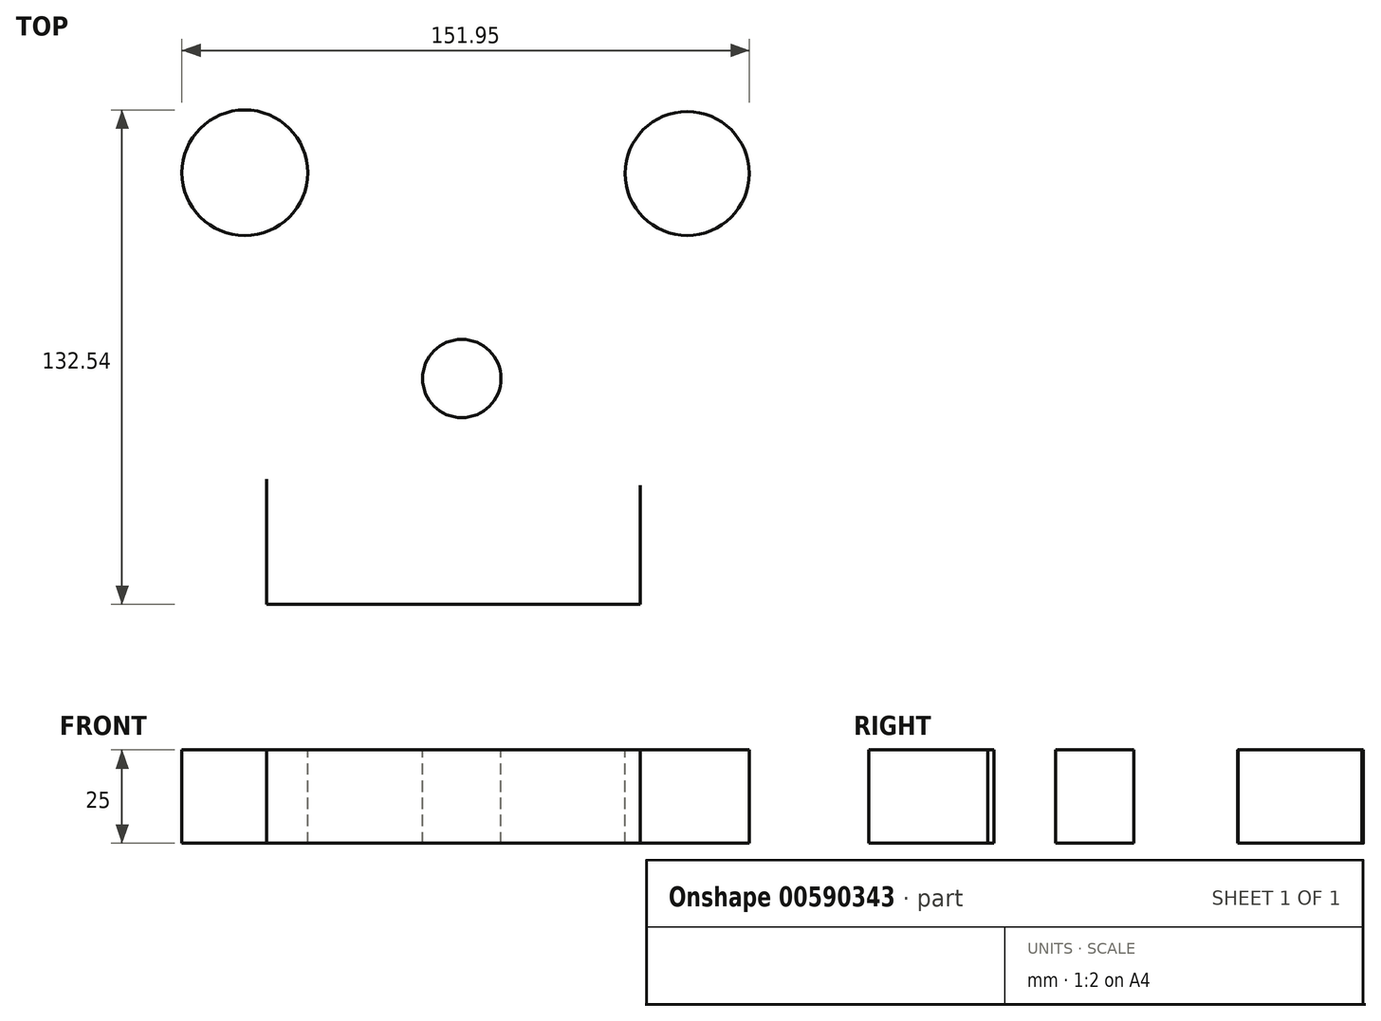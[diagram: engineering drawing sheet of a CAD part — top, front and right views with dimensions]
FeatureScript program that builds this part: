
annotation { "Feature Type Name" : "Feature", "Feature Type Description" : "" }
export const myFeature = defineFeature(function(context is Context, id is Id, definition is map)
    precondition{}
    {
        {
            var Q0;
            Q0=qCreatedBy(makeId("Top.planeOp"),FACE);
            var sketch = newSketch(context, id + "F0", { "sketchPlane" : qUnion([Q0])});
            skCircle(sketch, "E0", {"center": v(-58.13, 55.14) * mm, "radius": 16.83 * mm});
            skCircle(sketch, "E1", {"center": v(60.37, 54.96) * mm, "radius": 16.62 * mm});
            skCircle(sketch, "E2", {"center": v(0, 0) * mm, "radius": 10.5 * mm});
            skLineSegment(sketch, "E3", {"start": v(-52.28, -26.97) * mm, "end": v(-52.28, -60.56) * mm});
            skLineSegment(sketch, "E4", {"start": v(-52.28, -60.56) * mm, "end": v(47.74, -60.56) * mm});
            skLineSegment(sketch, "E5", {"start": v(47.74, -60.56) * mm, "end": v(47.74, -28.64) * mm});
            skSolve(sketch);
        }
        {
            var Q0;
            Q0=sQuery(id+"F0.wireOp",EDGE,"E3");
            var Q1;
            Q1=sQuery(id+"F0.wireOp",EDGE,"E4");
            var Q2;
            Q2=sQuery(id+"F0.wireOp",EDGE,"E5");
            var Q3;
            Q3=sQuery(id+"F0.wireOp",EDGE,"E2");
            var Q4;
            Q4=sQuery(id+"F0.wireOp",EDGE,"E0");
            var Q5;
            Q5=sQuery(id+"F0.wireOp",EDGE,"E1");
            extrude(context, id + "F1", {"bodyType" : ToolBodyType.SURFACE, "surfaceEntities" : qUnion([Q0, Q1, Q2, Q3, Q4, Q5]), "depth" : 25 * mm, "offsetDistance" : 25 * mm});
        }
    });
